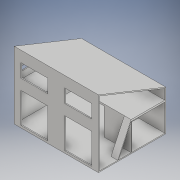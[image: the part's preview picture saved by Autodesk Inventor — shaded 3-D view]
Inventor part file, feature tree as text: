
AUTODESK INVENTOR PART (.ipt)
format: ipt  version: 2017 (Build 210142000, 142)  size: 269,312 bytes
history: native  units: in
note: dims shown in document units (in); Inventor stores cm internally (conversion verified against a paired STEP export)
features: sketch x15, extrude x14, plane x3, shell x1
ambient origin geometry x8: Origin, YZ Plane, XZ Plane, XY Plane, X Axis, Y Axis, Z Axis, Center Point
bodies: Solid1 (feature_tree)
feature tree (33):
  extrude  "main body"  Depth=240.0in
  extrude  "triangle"  Depth=96.0in
  shell  "Shell1"  Thickness=300.0in
  plane  "Work Plane1"
  extrude  "second floor"  Depth=96.0in
  plane  "Work Plane3"
  extrude  "bedroom"  Depth=6.0in TaperAngle=0.0deg
  extrude  "upper stairs"  TaperAngle=0.0deg  [1 undecoded]
  extrude  "main stairs"  Depth=84.0in
  sketch  "Sketch18"  dims[d21=6.0in d22=0.0in d23=0.0in]
  plane  "Work Plane4"
  extrude  "room wall 1"  TaperAngle=0.0deg  [1 undecoded]
  extrude  "room wall 2"  Depth=36.0in
  extrude  "outer wall"  Depth=24.0in TaperAngle=0.0deg
  sketch  "Sketch24"  dims[d52=54.0in d53=2.0in d54=0.0in]
  extrude  "side window 1"  Depth=24.0in TaperAngle=0.0deg
  sketch  "Sketch30"  dims[d73=8.0in d74=24.0in d78=36.0in d79=16.135in d81=12.0in d82=1.0in d83=0.0in d95=24.0in d100=3.5in d101=0.0in d102=3.5in d103=0.0in d105=96.0in d106=24.0in d107=24.0in d118=48.0in d119=0.7874in d121=156.0in d122=0.3937in d124=12.0in d126=3.5in d127=0.0in d130=3.5in d131=0.0in]
  extrude  "my WALL"  Depth=2.0in TaperAngle=0.0deg
  extrude  "other side window 1"  Depth=2.0in TaperAngle=0.0deg
  extrude  "front bottom windows"  Depth=96.0in
  extrude  "front top windows"  Depth=108.0in
  sketch  "Sketch1"  dims[d0=300.0in d1=240.0in]
  sketch  "Sketch3"  dims[d2=144.0in d3=0.0in d4=96.0in d5=300.0in d6=0.0in]
  sketch  "Sketch6"  dims[d7=3.5in d8=96.0in]
  sketch  "Sketch8"  dims[d12=120.0in d13=6.0in d14=0.0in]
  sketch  "Sketch16"  dims[d16=24.0in d17=0.0in]
  sketch  "Sketch17"  dims[d19=0.0in d20=84.0in]
  sketch  "Sketch20"  dims[d39=24.0in d40=36.0in]
  sketch  "Sketch21"  dims[d42=0.0in d43=24.0in d44=0.0in]
  sketch  "Sketch23"  dims[d46=0.7902in d48=24.0in d49=0.0in]
  sketch  "Sketch26"  dims[d56=2.0in d57=0.0in d60=1.0in d61=0.0in]
  sketch  "Sketch28"  dims[d62=8.0in d63=96.0in]
  sketch  "Sketch29"  dims[d64=24.0in d65=108.0in]
note: 2 required parameter values undecoded (feature->parameter linkage not recoverable at this tier; creation-order binding heuristic only, values carry confidence <= 0.55)
